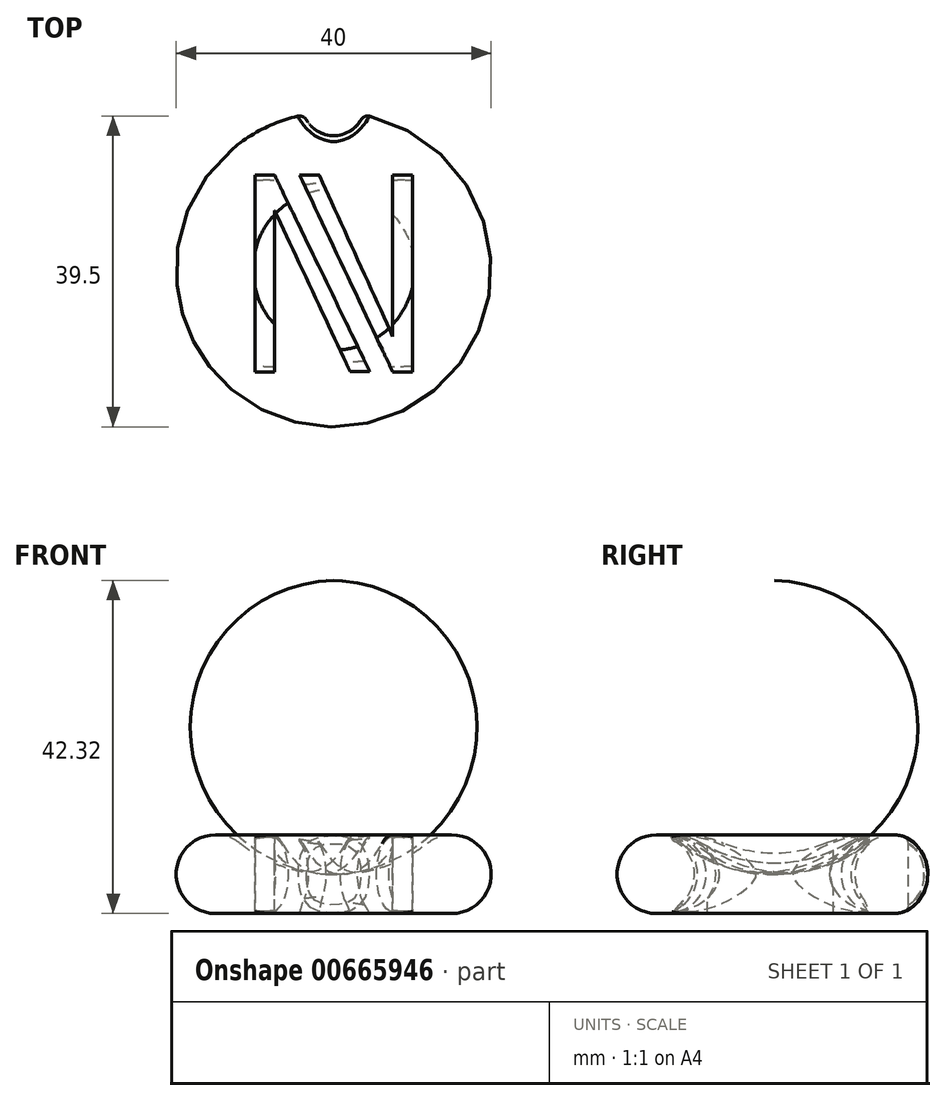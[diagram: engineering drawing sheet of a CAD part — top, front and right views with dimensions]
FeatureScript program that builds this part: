
annotation { "Feature Type Name" : "Feature", "Feature Type Description" : "" }
export const myFeature = defineFeature(function(context is Context, id is Id, definition is map)
    precondition{}
    {
        {
            var Q0;
            Q0=qCreatedBy(makeId("Front.planeOp"),FACE);
            var sketch = newSketch(context, id + "F0", { "sketchPlane" : qUnion([Q0])});
            skArc(sketch, "E0", {"start": v(-11.92, 8.94) * mm, "mid": v(-19.73, 6.63) * mm, "end": v(-15, 0) * mm});
            skArc(sketch, "E1", {"start": v(-11.92, 8.94) * mm, "mid": v(-6.3, 5.94) * mm, "end": v(0, 5) * mm});
            skLineSegment(sketch, "E2", {"start": v(0, 0) * mm, "end": v(-15, 0) * mm});
            skLineSegment(sketch, "E3", {"start": v(0, 0) * mm, "end": v(0, 5) * mm});
            skSolve(sketch);
        }
        {
            var Q0;
            Q0=makeQuery(id+"F0.imprint","IMPRINT",FACE,{"disambiguationData":[TD([[makeQuery(id+"F0.imprint","IMPRINT",EDGE,{"derivedFrom":sQuery(id+"F0.wireOp",EDGE,"E0")}),1.0]])]});
            var Q1;
            Q1=sQuery(id+"F0.wireOp",EDGE,"E3");
            revolve(context, id + "F1", {"entities" : qUnion([Q0]), "axis" : qUnion([Q1]), "revolveType" : RevolveType.FULL});
        }
        {
            var Q0;
            Q0=qCreatedBy(makeId("Top.planeOp"),FACE);
            cPlane(context, id + "F2", {"entities" : qUnion([Q0]), "cplaneType" : CPlaneType.OFFSET, "offset" : 10 * mm, "width" : 150 * mm, "height" : 150 * mm});
        }
        {
            var Q0;
            Q0=qCreatedBy(id+"F2.planeOp",FACE);
            var sketch = newSketch(context, id + "F3", { "sketchPlane" : qUnion([Q0])});
            skLineSegment(sketch, "E4.bottom", {"start": v(-10, 12) * mm, "end": v(-7.5, 12) * mm});
            skLineSegment(sketch, "E4.top", {"start": v(-10, -13) * mm, "end": v(-7.5, -13) * mm});
            skLineSegment(sketch, "E4.left", {"start": v(-10, 12) * mm, "end": v(-10, -13) * mm});
            skLineSegment(sketch, "E4.right", {"start": v(-7.5, 7.5) * mm, "end": v(-7.5, -13) * mm});
            skLineSegment(sketch, "E5", {"start": v(-7.5, 12) * mm, "end": v(4.59, -12.97) * mm});
            skLineSegment(sketch, "E6", {"start": v(2.09, -12.97) * mm, "end": v(-7.5, 7.5) * mm});
            skLineSegment(sketch, "E7", {"start": v(-1.83, 12) * mm, "end": v(-4.33, 12) * mm});
            skLineSegment(sketch, "E8.bottom", {"start": v(7.5, 12) * mm, "end": v(10, 12) * mm});
            skLineSegment(sketch, "E8.top", {"start": v(7.5, -13) * mm, "end": v(10, -13) * mm});
            skLineSegment(sketch, "E8.left", {"start": v(7.5, 12) * mm, "end": v(7.5, -8.5) * mm});
            skLineSegment(sketch, "E8.right", {"start": v(10, 12) * mm, "end": v(10, -13) * mm});
            skLineSegment(sketch, "E9", {"start": v(-1.83, 12) * mm, "end": v(7.5, -8.5) * mm});
            skLineSegment(sketch, "E10", {"start": v(-4.33, 12) * mm, "end": v(7.5, -13) * mm});
            skLineSegment(sketch, "E11", {"start": v(2.09, -12.97) * mm, "end": v(4.59, -12.97) * mm});
            skSolve(sketch);
        }
        {
            var Q0;
            Q0 = qSketchRegion(id + "F3", true);
            extrude(context, id + "F4", {"entities" : qUnion([Q0]), "operationType" : NewBodyOperationType.REMOVE, "oppositeDirection" : true, "depth" : 25 * mm, "offsetDistance" : 25 * mm});
        }
        {
            var Q0;
            Q0=qCreatedBy(makeId("Front.planeOp"),FACE);
            var sketch = newSketch(context, id + "F5", { "sketchPlane" : qUnion([Q0])});
            skCircle(sketch, "E12", {"center": v(-15, 5) * mm, "radius": 4.75 * mm});
            skSolve(sketch);
        }
        {
            var Q0;
            Q0 = qSketchRegion(id + "F5", true);
            var Q1;
            Q1=sQuery(id+"F0.wireOp",EDGE,"E3");
            revolve(context, id + "F6", {"operationType" : NewBodyOperationType.ADD, "entities" : qUnion([Q0]), "axis" : qUnion([Q1]), "revolveType" : RevolveType.FULL});
        }
        {
            var Q0;
            Q0=qCreatedBy(id+"F2.planeOp",FACE);
            var sketch = newSketch(context, id + "F7", { "sketchPlane" : qUnion([Q0])});
            skCircle(sketch, "E13", {"center": v(0, 21) * mm, "radius": 4 * mm});
            skSolve(sketch);
        }
        {
            var Q0;
            Q0 = qSketchRegion(id + "F7", true);
            extrude(context, id + "F8", {"entities" : qUnion([Q0]), "operationType" : NewBodyOperationType.REMOVE, "oppositeDirection" : true, "depth" : 25 * mm, "offsetDistance" : 25 * mm});
        }
        {
            var Q0;
            Q0=makeQuery(id+"F8.boolean.opBoolean","INTERSECT",EDGE,{"derivedFrom":[makeQuery(id+"F1.opRevolve","SWEPT_FACE",FACE,{"disambiguationData":[OSD([sQuery(id+"F0.wireOp",EDGE,"E0")])]}),makeQuery(id+"F8.opExtrude","SWEPT_FACE",FACE,{"disambiguationData":[OSD([sQuery(id+"F7.wireOp",EDGE,"E13")])]})]});
            fillet(context, id + "F9", {"entities" : qUnion([Q0]), "radius" : 1 * mm, "tangentPropagation" : true, "allowEdgeOverflow" : false});
        }
        {
            var Q0;
            Q0=makeQuery(id+"F6.boolean.opBoolean","INTERSECT",EDGE,{"disambiguationData":[OD(0.0)],"derivedFrom":[makeQuery(id+"F4.boolean.opBoolean","COPY",FACE,{"derivedFrom":makeQuery(id+"F4.opExtrude","SWEPT_FACE",FACE,{"disambiguationData":[OSD([sQuery(id+"F3.wireOp",EDGE,"E4.top")])]})}),makeQuery(id+"F6.opRevolve","SWEPT_FACE",FACE,{"disambiguationData":[OSD([sQuery(id+"F5.wireOp",EDGE,"E12")])]})]});
            var Q1;
            Q1=makeQuery(id+"F6.boolean.opBoolean","INTERSECT",EDGE,{"disambiguationData":[OD(0.0)],"derivedFrom":[makeQuery(id+"F4.boolean.opBoolean","COPY",FACE,{"derivedFrom":makeQuery(id+"F4.opExtrude","SWEPT_FACE",FACE,{"disambiguationData":[OSD([sQuery(id+"F3.wireOp",EDGE,"E4.bottom")])]})}),makeQuery(id+"F6.opRevolve","SWEPT_FACE",FACE,{"disambiguationData":[OSD([sQuery(id+"F5.wireOp",EDGE,"E12")])]})]});
            var Q2;
            Q2=makeQuery(id+"F6.boolean.opBoolean","INTERSECT",EDGE,{"disambiguationData":[OD(0.0)],"derivedFrom":[makeQuery(id+"F4.boolean.opBoolean","COPY",FACE,{"derivedFrom":makeQuery(id+"F4.opExtrude","SWEPT_FACE",FACE,{"disambiguationData":[OSD([sQuery(id+"F3.wireOp",EDGE,"E8.bottom")])]})}),makeQuery(id+"F6.opRevolve","SWEPT_FACE",FACE,{"disambiguationData":[OSD([sQuery(id+"F5.wireOp",EDGE,"E12")])]})]});
            var Q3;
            Q3=makeQuery(id+"F6.boolean.opBoolean","INTERSECT",EDGE,{"disambiguationData":[OD(0.0)],"derivedFrom":[makeQuery(id+"F4.boolean.opBoolean","COPY",FACE,{"derivedFrom":makeQuery(id+"F4.opExtrude","SWEPT_FACE",FACE,{"disambiguationData":[OSD([sQuery(id+"F3.wireOp",EDGE,"E8.top")])]})}),makeQuery(id+"F6.opRevolve","SWEPT_FACE",FACE,{"disambiguationData":[OSD([sQuery(id+"F5.wireOp",EDGE,"E12")])]})]});
            fillet(context, id + "F10", {"entities" : qUnion([Q0, Q1, Q2, Q3]), "radius" : 1 * mm, "tangentPropagation" : true, "allowEdgeOverflow" : false});
        }
        {
            var Q0;
            Q0=makeQuery(id+"F6.boolean.opBoolean","INTERSECT",EDGE,{"disambiguationData":[OD(1.0)],"derivedFrom":[makeQuery(id+"F4.boolean.opBoolean","COPY",FACE,{"derivedFrom":makeQuery(id+"F4.opExtrude","SWEPT_FACE",FACE,{"disambiguationData":[OSD([sQuery(id+"F3.wireOp",EDGE,"E11")])]})}),makeQuery(id+"F6.opRevolve","SWEPT_FACE",FACE,{"disambiguationData":[OSD([sQuery(id+"F5.wireOp",EDGE,"E12")])]})]});
            var Q1;
            Q1=makeQuery(id+"F6.boolean.opBoolean","INTERSECT",EDGE,{"disambiguationData":[OD(1.0)],"derivedFrom":[makeQuery(id+"F4.boolean.opBoolean","COPY",FACE,{"derivedFrom":makeQuery(id+"F4.opExtrude","SWEPT_FACE",FACE,{"disambiguationData":[OSD([sQuery(id+"F3.wireOp",EDGE,"E7")])]})}),makeQuery(id+"F6.opRevolve","SWEPT_FACE",FACE,{"disambiguationData":[OSD([sQuery(id+"F5.wireOp",EDGE,"E12")])]})]});
            fillet(context, id + "F11", {"entities" : qUnion([Q0, Q1]), "radius" : 5 * mm, "tangentPropagation" : true, "allowEdgeOverflow" : false});
        }
    });
